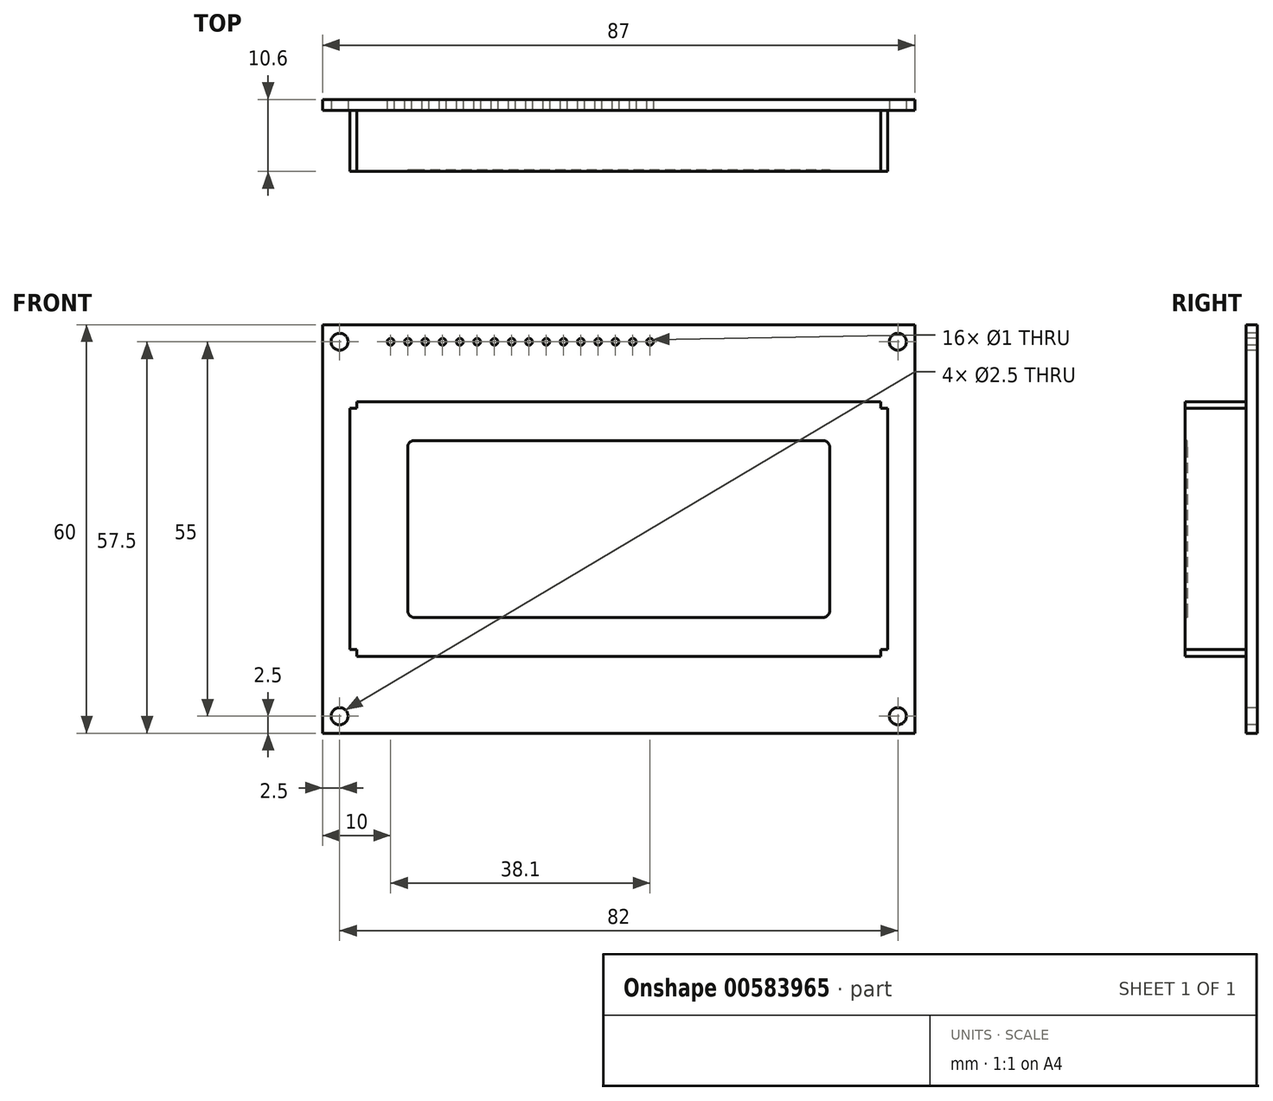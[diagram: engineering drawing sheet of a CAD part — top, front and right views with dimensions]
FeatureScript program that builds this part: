
annotation { "Feature Type Name" : "Feature", "Feature Type Description" : "" }
export const myFeature = defineFeature(function(context is Context, id is Id, definition is map)
    precondition{}
    {
        {
            var Q0;
            Q0=qCreatedBy(makeId("Front.planeOp"),FACE);
            var sketch = newSketch(context, id + "F0", { "sketchPlane" : qUnion([Q0])});
            skLineSegment(sketch, "E0.bottom", {"start": v(-39.5, 18.7) * mm, "end": v(39.5, 18.7) * mm});
            skLineSegment(sketch, "E0.top", {"start": v(-39.5, -18.7) * mm, "end": v(39.5, -18.7) * mm});
            skLineSegment(sketch, "E0.left", {"start": v(-39.5, 18.7) * mm, "end": v(-39.5, -18.7) * mm});
            skLineSegment(sketch, "E0.right", {"start": v(39.5, 18.7) * mm, "end": v(39.5, -18.7) * mm});
            skPoint(sketch, "E0.middle", {"position": v(0, 0) * mm});
            skSolve(sketch);
        }
        {
            var Q0;
            Q0=makeQuery(id+"F0.imprint","IMPRINT",FACE,{"disambiguationData":[TD([[makeQuery(id+"F0.imprint","IMPRINT",EDGE,{"derivedFrom":sQuery(id+"F0.wireOp",EDGE,"E0.bottom")}),-1.0]])]});
            extrude(context, id + "F1", {"entities" : qUnion([Q0]), "depth" : 9 * mm, "offsetDistance" : 25.4 * mm});
        }
        {
            var Q0;
            Q0=makeQuery(id+"F1.opExtrude","CAP_FACE",FACE,{"disambiguationData":[OSD([sQuery(id+"F0.wireOp",EDGE,"E0.bottom"),sQuery(id+"F0.wireOp",EDGE,"E0.top"),sQuery(id+"F0.wireOp",EDGE,"E0.left"),sQuery(id+"F0.wireOp",EDGE,"E0.right")])],"isStart":false});
            var sketch = newSketch(context, id + "F2", { "sketchPlane" : qUnion([Q0])});
            skLineSegment(sketch, "E1.bottom", {"start": v(-31, 13) * mm, "end": v(31, 13) * mm});
            skLineSegment(sketch, "E1.top", {"start": v(-31, -13) * mm, "end": v(31, -13) * mm});
            skLineSegment(sketch, "E1.left", {"start": v(-31, 13) * mm, "end": v(-31, -13) * mm});
            skLineSegment(sketch, "E1.right", {"start": v(31, 13) * mm, "end": v(31, -13) * mm});
            skPoint(sketch, "E1.middle", {"position": v(0, 0) * mm});
            skSolve(sketch);
        }
        {
            var Q0;
            Q0 = qSketchRegion(id + "F2", true);
            extrude(context, id + "F3", {"entities" : qUnion([Q0]), "operationType" : NewBodyOperationType.REMOVE, "oppositeDirection" : true, "depth" : .3 * mm, "offsetDistance" : 25.4 * mm});
        }
        {
            var Q0;
            Q0=makeQuery(id+"F3.boolean.opBoolean","COPY",EDGE,{"derivedFrom":makeQuery(id+"F3.opExtrude","SWEPT_EDGE",EDGE,{"disambiguationData":[OSD([sQuery(id+"F2.wireOp",EDGE,"E1.bottom"),sQuery(id+"F2.wireOp",EDGE,"E1.left")])]})});
            var Q1;
            Q1=makeQuery(id+"F3.boolean.opBoolean","COPY",EDGE,{"derivedFrom":makeQuery(id+"F3.opExtrude","SWEPT_EDGE",EDGE,{"disambiguationData":[OSD([sQuery(id+"F2.wireOp",EDGE,"E1.bottom"),sQuery(id+"F2.wireOp",EDGE,"E1.right")])]})});
            var Q2;
            Q2=makeQuery(id+"F3.boolean.opBoolean","COPY",EDGE,{"derivedFrom":makeQuery(id+"F3.opExtrude","SWEPT_EDGE",EDGE,{"disambiguationData":[OSD([sQuery(id+"F2.wireOp",EDGE,"E1.top"),sQuery(id+"F2.wireOp",EDGE,"E1.right")])]})});
            var Q3;
            Q3=makeQuery(id+"F3.boolean.opBoolean","COPY",EDGE,{"derivedFrom":makeQuery(id+"F3.opExtrude","SWEPT_EDGE",EDGE,{"disambiguationData":[OSD([sQuery(id+"F2.wireOp",EDGE,"E1.top"),sQuery(id+"F2.wireOp",EDGE,"E1.left")])]})});
            fillet(context, id + "F4", {"entities" : qUnion([Q0, Q1, Q2, Q3]), "radius" : 1 * mm, "tangentPropagation" : true, "allowEdgeOverflow" : false});
        }
        {
            var Q0;
            Q0=makeQuery(id+"F1.opExtrude","CAP_FACE",FACE,{"disambiguationData":[OSD([sQuery(id+"F0.wireOp",EDGE,"E0.bottom"),sQuery(id+"F0.wireOp",EDGE,"E0.top"),sQuery(id+"F0.wireOp",EDGE,"E0.left"),sQuery(id+"F0.wireOp",EDGE,"E0.right")])],"isStart":false});
            var sketch = newSketch(context, id + "F5", { "sketchPlane" : qUnion([Q0])});
            skLineSegment(sketch, "E2.bottom", {"start": v(-39.5, -18.7) * mm, "end": v(-38.5, -18.7) * mm});
            skLineSegment(sketch, "E2.top", {"start": v(-39.5, -17.7) * mm, "end": v(-38.5, -17.7) * mm});
            skLineSegment(sketch, "E2.left", {"start": v(-39.5, -18.7) * mm, "end": v(-39.5, -17.7) * mm});
            skLineSegment(sketch, "E2.right", {"start": v(-38.5, -18.7) * mm, "end": v(-38.5, -17.7) * mm});
            skLineSegment(sketch, "E3.bottom", {"start": v(39.5, -18.7) * mm, "end": v(38.5, -18.7) * mm});
            skLineSegment(sketch, "E3.top", {"start": v(39.5, -17.7) * mm, "end": v(38.5, -17.7) * mm});
            skLineSegment(sketch, "E3.left", {"start": v(39.5, -18.7) * mm, "end": v(39.5, -17.7) * mm});
            skLineSegment(sketch, "E3.right", {"start": v(38.5, -18.7) * mm, "end": v(38.5, -17.7) * mm});
            skLineSegment(sketch, "E4.bottom", {"start": v(39.5, 18.7) * mm, "end": v(38.5, 18.7) * mm});
            skLineSegment(sketch, "E4.top", {"start": v(39.5, 17.7) * mm, "end": v(38.5, 17.7) * mm});
            skLineSegment(sketch, "E4.left", {"start": v(39.5, 18.7) * mm, "end": v(39.5, 17.7) * mm});
            skLineSegment(sketch, "E4.right", {"start": v(38.5, 18.7) * mm, "end": v(38.5, 17.7) * mm});
            skLineSegment(sketch, "E5.bottom", {"start": v(-39.5, 18.7) * mm, "end": v(-38.5, 18.7) * mm});
            skLineSegment(sketch, "E5.top", {"start": v(-39.5, 17.7) * mm, "end": v(-38.5, 17.7) * mm});
            skLineSegment(sketch, "E5.left", {"start": v(-39.5, 18.7) * mm, "end": v(-39.5, 17.7) * mm});
            skLineSegment(sketch, "E5.right", {"start": v(-38.5, 18.7) * mm, "end": v(-38.5, 17.7) * mm});
            skSolve(sketch);
        }
        {
            var Q0;
            Q0 = qSketchRegion(id + "F5", true);
            extrude(context, id + "F6", {"entities" : qUnion([Q0]), "operationType" : NewBodyOperationType.REMOVE, "oppositeDirection" : true, "depth" : 25.4 * mm, "offsetDistance" : 25.4 * mm});
        }
        {
            var Q0;
            Q0=makeQuery(id+"F1.opExtrude","CAP_FACE",FACE,{"disambiguationData":[OSD([sQuery(id+"F0.wireOp",EDGE,"E0.bottom"),sQuery(id+"F0.wireOp",EDGE,"E0.top"),sQuery(id+"F0.wireOp",EDGE,"E0.left"),sQuery(id+"F0.wireOp",EDGE,"E0.right")])],"isStart":true});
            var sketch = newSketch(context, id + "F7", { "sketchPlane" : qUnion([Q0])});
            skLineSegment(sketch, "E6.bottom", {"start": v(-43.5, 30) * mm, "end": v(43.5, 30) * mm});
            skLineSegment(sketch, "E6.top", {"start": v(-43.5, -30) * mm, "end": v(43.5, -30) * mm});
            skLineSegment(sketch, "E6.left", {"start": v(-43.5, 30) * mm, "end": v(-43.5, -30) * mm});
            skLineSegment(sketch, "E6.right", {"start": v(43.5, 30) * mm, "end": v(43.5, -30) * mm});
            skSolve(sketch);
        }
        {
            var Q0;
            Q0 = qSketchRegion(id + "F7", true);
            extrude(context, id + "F8", {"entities" : qUnion([Q0]), "operationType" : NewBodyOperationType.ADD, "depth" : 1.6 * mm, "offsetDistance" : 25.4 * mm});
        }
        {
            var Q0;
            Q0=makeQuery(id+"F8.opExtrude","CAP_FACE",FACE,{"disambiguationData":[OSD([sQuery(id+"F7.wireOp",EDGE,"E6.bottom"),sQuery(id+"F7.wireOp",EDGE,"E6.top"),sQuery(id+"F7.wireOp",EDGE,"E6.left"),sQuery(id+"F7.wireOp",EDGE,"E6.right")])],"isStart":true});
            var sketch = newSketch(context, id + "F9", { "sketchPlane" : qUnion([Q0])});
            skPoint(sketch, "E7", {"position": v(-41, 27.5) * mm});
            skPoint(sketch, "E8", {"position": v(41, 27.5) * mm});
            skPoint(sketch, "E9", {"position": v(41, -27.5) * mm});
            skPoint(sketch, "E10", {"position": v(-41, -27.5) * mm});
            skSolve(sketch);
        }
        {
            var Q0;
            Q0=sQuery(id+"F9.wireOp",VERTEX,"E7");
            var Q1;
            Q1=sQuery(id+"F9.wireOp",VERTEX,"E10");
            var Q2;
            Q2=sQuery(id+"F9.wireOp",VERTEX,"E8");
            var Q3;
            Q3=sQuery(id+"F9.wireOp",VERTEX,"E9");
            var Q4;
            Q4=makeQuery(id+"F1.opExtrude","SWEPT_BODY",BODY,{"disambiguationData":[OSD([sQuery(id+"F0.wireOp",EDGE,"E0.bottom"),sQuery(id+"F0.wireOp",EDGE,"E0.top"),sQuery(id+"F0.wireOp",EDGE,"E0.left"),sQuery(id+"F0.wireOp",EDGE,"E0.right")])]});
            hole(context, id + "F10", {"style" : HoleStyle.SIMPLE, "endStyle" : HoleEndStyle.THROUGH, "holeDiameter" : 2.5 * mm, "majorDiameter" : 6.35 * mm, "isTappedThrough" : true, "tappedDepth" : 12.7 * mm, "tapClearance" : 3, "locations" : qUnion([Q0, Q1, Q2, Q3]), "scope" : qUnion([Q4])});
        }
        {
            var Q0;
            Q0=makeQuery(id+"F8.opExtrude","CAP_FACE",FACE,{"disambiguationData":[OSD([sQuery(id+"F7.wireOp",EDGE,"E6.bottom"),sQuery(id+"F7.wireOp",EDGE,"E6.top"),sQuery(id+"F7.wireOp",EDGE,"E6.left"),sQuery(id+"F7.wireOp",EDGE,"E6.right")])],"isStart":true});
            var sketch = newSketch(context, id + "F11", { "sketchPlane" : qUnion([Q0])});
            skPoint(sketch, "E11", {"position": v(-33.5, 27.5) * mm});
            skPoint(sketch, "E12.1.0.0", {"position": v(-30.96, 27.5) * mm});
            skPoint(sketch, "E12.2.0.0", {"position": v(-28.42, 27.5) * mm});
            skPoint(sketch, "E12.3.0.0", {"position": v(-25.88, 27.5) * mm});
            skPoint(sketch, "E12.4.0.0", {"position": v(-23.34, 27.5) * mm});
            skPoint(sketch, "E12.5.0.0", {"position": v(-20.8, 27.5) * mm});
            skPoint(sketch, "E12.6.0.0", {"position": v(-18.26, 27.5) * mm});
            skPoint(sketch, "E12.7.0.0", {"position": v(-15.72, 27.5) * mm});
            skPoint(sketch, "E12.8.0.0", {"position": v(-13.18, 27.5) * mm});
            skPoint(sketch, "E12.9.0.0", {"position": v(-10.64, 27.5) * mm});
            skPoint(sketch, "E12.10.0.0", {"position": v(-8.1, 27.5) * mm});
            skPoint(sketch, "E12.11.0.0", {"position": v(-5.56, 27.5) * mm});
            skPoint(sketch, "E12.12.0.0", {"position": v(-3.02, 27.5) * mm});
            skPoint(sketch, "E12.13.0.0", {"position": v(-0.48, 27.5) * mm});
            skPoint(sketch, "E12.14.0.0", {"position": v(2.06, 27.5) * mm});
            skPoint(sketch, "E12.15.0.0", {"position": v(4.6, 27.5) * mm});
            skLineSegment(sketch, "E12.direction1", {"start": v(-33.5, 27.5) * mm, "end": v(-30.96, 27.5) * mm, "construction": true});
            skSolve(sketch);
        }
        {
            var Q0;
            Q0=sQuery(id+"F11.wireOp",VERTEX,"E11");
            var Q1;
            Q1=sQuery(id+"F11.wireOp",VERTEX,"E12.1.0.0");
            var Q2;
            Q2=sQuery(id+"F11.wireOp",VERTEX,"E12.2.0.0");
            var Q3;
            Q3=sQuery(id+"F11.wireOp",VERTEX,"E12.3.0.0");
            var Q4;
            Q4=sQuery(id+"F11.wireOp",VERTEX,"E12.4.0.0");
            var Q5;
            Q5=sQuery(id+"F11.wireOp",VERTEX,"E12.5.0.0");
            var Q6;
            Q6=sQuery(id+"F11.wireOp",VERTEX,"E12.6.0.0");
            var Q7;
            Q7=sQuery(id+"F11.wireOp",VERTEX,"E12.7.0.0");
            var Q8;
            Q8=sQuery(id+"F11.wireOp",VERTEX,"E12.8.0.0");
            var Q9;
            Q9=sQuery(id+"F11.wireOp",VERTEX,"E12.9.0.0");
            var Q10;
            Q10=sQuery(id+"F11.wireOp",VERTEX,"E12.10.0.0");
            var Q11;
            Q11=sQuery(id+"F11.wireOp",VERTEX,"E12.11.0.0");
            var Q12;
            Q12=sQuery(id+"F11.wireOp",VERTEX,"E12.12.0.0");
            var Q13;
            Q13=sQuery(id+"F11.wireOp",VERTEX,"E12.13.0.0");
            var Q14;
            Q14=sQuery(id+"F11.wireOp",VERTEX,"E12.14.0.0");
            var Q15;
            Q15=sQuery(id+"F11.wireOp",VERTEX,"E12.15.0.0");
            var Q16;
            Q16=makeQuery(id+"F1.opExtrude","SWEPT_BODY",BODY,{"disambiguationData":[OSD([sQuery(id+"F0.wireOp",EDGE,"E0.bottom"),sQuery(id+"F0.wireOp",EDGE,"E0.top"),sQuery(id+"F0.wireOp",EDGE,"E0.left"),sQuery(id+"F0.wireOp",EDGE,"E0.right")])]});
            hole(context, id + "F12", {"style" : HoleStyle.SIMPLE, "endStyle" : HoleEndStyle.THROUGH, "holeDiameter" : 1 * mm, "majorDiameter" : 6.35 * mm, "isTappedThrough" : true, "tappedDepth" : 12.7 * mm, "tapClearance" : 3, "locations" : qUnion([Q0, Q1, Q2, Q3, Q4, Q5, Q6, Q7, Q8, Q9, Q10, Q11, Q12, Q13, Q14, Q15]), "scope" : qUnion([Q16])});
        }
    });
